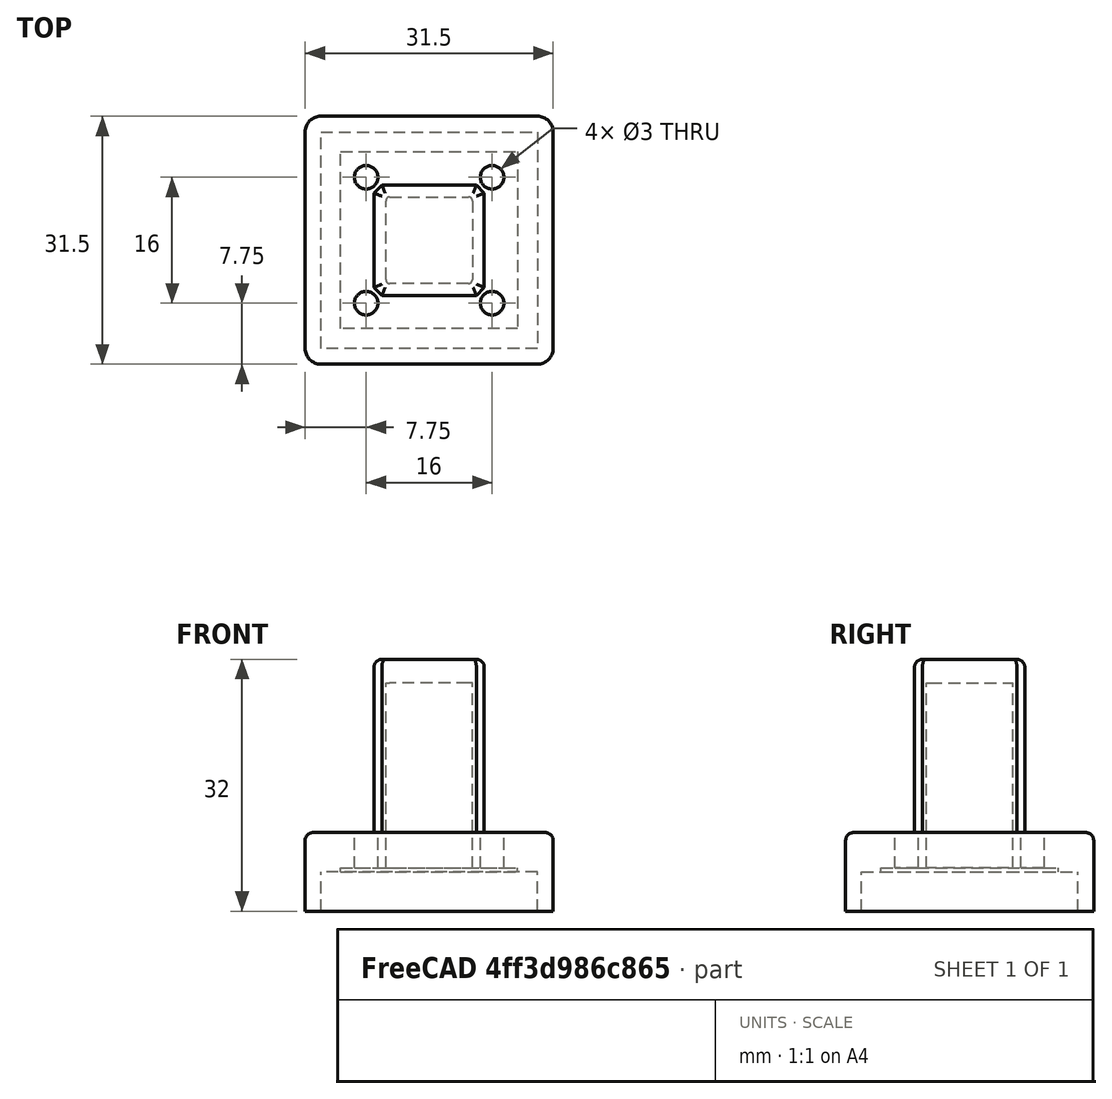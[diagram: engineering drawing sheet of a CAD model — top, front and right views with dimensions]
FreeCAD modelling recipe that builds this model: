
FCSTD DOCUMENT  (FreeCAD 1.1R44874 (Git))
Label: hood1slim_10x10x20_B
objects: Sketcher::SketchObject×7, PartDesign::Pocket×3, PartDesign::Pad×2, PartDesign::Fillet×2, App::Point×1, PartDesign::Hole×1, PartDesign::Body×1, Mesh::Feature×1
note: 39 computed .brp shape members not serialized (recipe doc carries the construction recipe); baked Part::Feature solids carry a one-line shape summary decoded from their .brp

FEATURE [App::Point] Origin001
  Role = Origin
FEATURE [Sketcher::SketchObject] Sketch
  ArcFitTolerance = 1e-06
  AttachmentSupport = -> [Origin]
  ExternalTypes = [0]
  FullyConstrained = true
  MakeInternals = false
  MapMode = 5
  _ExternalGeoVersion = 1
  sketch-geometry (13):
    g0: LineSegment StartX=-13.75 StartY=-15.75 StartZ=0 EndX=13.75 EndY=-15.75 EndZ=0
    g1: LineSegment StartX=15.75 StartY=-13.75 StartZ=0 EndX=15.75 EndY=13.75 EndZ=0
    g2: LineSegment StartX=13.75 StartY=15.75 StartZ=0 EndX=-13.75 EndY=15.75 EndZ=0
    g3: LineSegment StartX=-15.75 StartY=13.75 StartZ=0 EndX=-15.75 EndY=-13.75 EndZ=0
    g4: GeomPoint [constr] X=0 Y=0 Z=0
    g5: ArcOfCircle CenterX=-13.75 CenterY=13.75 CenterZ=0 NormalX=0 NormalY=0 NormalZ=1 AngleXU=0 Radius=2 StartAngle=1.5708 EndAngle=3.14159
    g6: GeomPoint [constr] X=-15.75 Y=15.75 Z=0
    g7: ArcOfCircle CenterX=13.75 CenterY=13.75 CenterZ=0 NormalX=0 NormalY=0 NormalZ=1 AngleXU=0 Radius=2 StartAngle=0 EndAngle=1.5708
    g8: GeomPoint [constr] X=15.75 Y=15.75 Z=0
    g9: ArcOfCircle CenterX=13.75 CenterY=-13.75 CenterZ=0 NormalX=0 NormalY=0 NormalZ=1 AngleXU=0 Radius=2 StartAngle=4.71239 EndAngle=6.28319
    g10: GeomPoint [constr] X=15.75 Y=-15.75 Z=0
    g11: ArcOfCircle CenterX=-13.75 CenterY=-13.75 CenterZ=0 NormalX=0 NormalY=0 NormalZ=1 AngleXU=0 Radius=2 StartAngle=3.14159 EndAngle=4.71239
    g12: GeomPoint [constr] X=-15.75 Y=-15.75 Z=0
  constraints (28):
    c: Horizontal(g0)
    c: Horizontal(g2)
    c: Vertical(g1)
    c: Vertical(g3)
    c: Symmetric(g8,g12,g4)
    c: Distance(g10,g12) = 31.5
    c: Distance(g12,g6) = 31.5
    c: Coincident(g4,g-1)
    c: PointOnObject(g6,g3)
    c: PointOnObject(g6,g2)
    c: Tangent(g3,g5) = -1.5708
    c: Tangent(g2,g5) = -1.5708
    c: Radius(g5) = 2
    c: PointOnObject(g8,g1)
    c: PointOnObject(g8,g2)
    c: Tangent(g1,g7) = -1.5708
    c: Tangent(g2,g7) = -1.5708
    c: PointOnObject(g10,g1)
    c: PointOnObject(g10,g0)
    c: Tangent(g1,g9) = -1.5708
    c: Tangent(g0,g9) = -1.5708
    c: PointOnObject(g12,g0)
    c: PointOnObject(g12,g3)
    c: Tangent(g0,g11) = -1.5708
    c: Tangent(g3,g11) = -1.5708
    c: Equal(g5,g7)
    c: Equal(g5,g11)
    c: Equal(g5,g9)
FEATURE [PartDesign::Pad] Pad
  Direction = (0,0,1)
  Length = 10
  Length2 = 10
  Profile = -> Sketch
  ReferenceAxis = -> Sketch [N_Axis]
  Refine = true
  SideType = 0
  Suppressed = false
  Type = 0
  Type2 = 0
FEATURE [Sketcher::SketchObject] Sketch001
  ArcFitTolerance = 1e-06
  AttachmentSupport = -> [Pad]
  ExternalTypes = [0]
  FullyConstrained = true
  MakeInternals = false
  MapMode = 5
  Placement = pos=(0,0,0) rot=(1,0,0;3.14159rad)
  _ExternalGeoVersion = 1
  sketch-geometry (5):
    g0: LineSegment StartX=-13.75 StartY=-13.75 StartZ=0 EndX=13.75 EndY=-13.75 EndZ=0
    g1: LineSegment StartX=13.75 StartY=-13.75 StartZ=0 EndX=13.75 EndY=13.75 EndZ=0
    g2: LineSegment StartX=13.75 StartY=13.75 StartZ=0 EndX=-13.75 EndY=13.75 EndZ=0
    g3: LineSegment StartX=-13.75 StartY=13.75 StartZ=0 EndX=-13.75 EndY=-13.75 EndZ=0
    g4: GeomPoint [constr] X=0 Y=0 Z=0
  constraints (12):
    c: Coincident(g0,g1)
    c: Coincident(g1,g2)
    c: Coincident(g2,g3)
    c: Coincident(g3,g0)
    c: Horizontal(g0)
    c: Horizontal(g2)
    c: Vertical(g1)
    c: Vertical(g3)
    c: Symmetric(g2,g0,g4)
    c: Distance(g1,g3) = 27.5
    c: Distance(g0,g2) = 27.5
    c: Coincident(g4,g-1)
FEATURE [PartDesign::Pocket] Pocket
  BaseFeature = -> Pad
  Direction = (0,0,1)
  Length = 5
  Length2 = 5
  Profile = -> Sketch001
  ReferenceAxis = -> Sketch001 [N_Axis]
  Refine = true
  SideType = 0
  Suppressed = false
  Type = 0
  Type2 = 0
FEATURE [Sketcher::SketchObject] Sketch002
  ArcFitTolerance = 1e-06
  AttachmentSupport = -> [Pocket]
  ExternalTypes = [0]
  FullyConstrained = true
  MakeInternals = false
  MapMode = 5
  Placement = pos=(0,0,5) rot=(1,0,0;3.14159rad)
  _ExternalGeoVersion = 1
  sketch-geometry (5):
    g0: LineSegment StartX=-11.25 StartY=-11.25 StartZ=0 EndX=11.25 EndY=-11.25 EndZ=0
    g1: LineSegment StartX=11.25 StartY=-11.25 StartZ=0 EndX=11.25 EndY=11.25 EndZ=0
    g2: LineSegment StartX=11.25 StartY=11.25 StartZ=0 EndX=-11.25 EndY=11.25 EndZ=0
    g3: LineSegment StartX=-11.25 StartY=11.25 StartZ=0 EndX=-11.25 EndY=-11.25 EndZ=0
    g4: GeomPoint [constr] X=0 Y=0 Z=0
  constraints (12):
    c: Coincident(g0,g1)
    c: Coincident(g1,g2)
    c: Coincident(g2,g3)
    c: Coincident(g3,g0)
    c: Horizontal(g0)
    c: Horizontal(g2)
    c: Vertical(g1)
    c: Vertical(g3)
    c: Symmetric(g2,g0,g4)
    c: Distance(g1,g3) = 22.5
    c: Distance(g0,g2) = 22.5
    c: Coincident(g4,g-1)
FEATURE [PartDesign::Pocket] Pocket001
  BaseFeature = -> Pocket
  Direction = (0,0,1)
  Length = 0.5
  Length2 = 5
  Profile = -> Sketch002
  ReferenceAxis = -> Sketch002 [N_Axis]
  Refine = true
  SideType = 0
  Suppressed = false
  Type = 0
  Type2 = 0
FEATURE [Sketcher::SketchObject] Sketch003
  ArcFitTolerance = 1e-06
  AttachmentSupport = -> [Pocket001]
  ExternalTypes = [0]
  FullyConstrained = true
  MakeInternals = false
  MapMode = 5
  Placement = pos=(0,0,5.5) rot=(1,0,0;3.14159rad)
  _ExternalGeoVersion = 1
  sketch-geometry (4):
    g0: Circle CenterX=8 CenterY=8 CenterZ=0 NormalX=0 NormalY=0 NormalZ=1 AngleXU=0 Radius=1.5
    g1: Circle CenterX=-8 CenterY=8 CenterZ=0 NormalX=0 NormalY=0 NormalZ=1 AngleXU=0 Radius=1.5
    g2: Circle CenterX=-8 CenterY=-8 CenterZ=0 NormalX=0 NormalY=0 NormalZ=1 AngleXU=0 Radius=1.5
    g3: Circle CenterX=8 CenterY=-8 CenterZ=0 NormalX=0 NormalY=0 NormalZ=1 AngleXU=0 Radius=1.5
  constraints (9):
    c: Diameter(g0) = 3
    c: DistanceY(g-1,g0) = 8
    c: DistanceX(g-1,g0) = 8
    c: Equal(g0,g1)
    c: Equal(g0,g2)
    c: Equal(g0,g3)
    c: Symmetric(g1,g3,g-1)
    c: Symmetric(g0,g3,g-1)
    c: Symmetric(g2,g3,g-2)
FEATURE [PartDesign::Hole] Hole
  BaseFeature = -> Pocket001
  BaseProfileType = 7
  CustomThreadClearance = 0
  Depth = 15
  DepthType = 0
  Diameter = 3
  DrillForDepth = false
  DrillPoint = 1
  DrillPointAngle = 118
  HoleCutCountersinkAngle = 90
  HoleCutCustomValues = false
  HoleCutDepth = 0
  HoleCutDiameter = 0
  HoleCutType = 0
  ModelThread = false
  Profile = -> Sketch003
  Refine = true
  Suppressed = false
  Tapered = false
  TaperedAngle = 90
  ThreadClass = 0
  ThreadDepth = 15
  ThreadDepthType = 0
  ThreadDiameter = 3
  ThreadDirection = 0
  ThreadFit = 0
  ThreadSize = 0
  ThreadType = 0
  Threaded = false
  UseCustomThreadClearance = false
FEATURE [Sketcher::SketchObject] Sketch004
  ArcFitTolerance = 1e-06
  AttachmentSupport = -> [Hole]
  ExternalGeometry = -> [Sketch002]
  ExternalTypes = [0,0,0,0]
  FullyConstrained = true
  MakeInternals = false
  MapMode = 5
  Placement = pos=(0,0,5.5) rot=(1,0,0;3.14159rad)
  _ExternalGeoVersion = 1
  sketch-geometry (21):
    g0: GeomPoint [constr] X=0 Y=0 Z=0
    g1: LineSegment StartX=-11.25 StartY=-5.5 StartZ=0 EndX=-11.25 EndY=5.5 EndZ=0
    g2: LineSegment StartX=-11.25 StartY=5.5 StartZ=0 EndX=-7 EndY=5.5 EndZ=0
    g3: LineSegment StartX=-5.5 StartY=7 StartZ=0 EndX=-5.5 EndY=11.25 EndZ=0
    g4: LineSegment StartX=-5.5 StartY=11.25 StartZ=0 EndX=5.5 EndY=11.25 EndZ=0
    g5: LineSegment StartX=5.5 StartY=11.25 StartZ=0 EndX=5.5 EndY=7 EndZ=0
    g6: LineSegment StartX=7 StartY=5.5 StartZ=0 EndX=11.25 EndY=5.5 EndZ=0
    g7: LineSegment StartX=11.25 StartY=5.5 StartZ=0 EndX=11.25 EndY=-5.5 EndZ=0
    g8: LineSegment StartX=11.25 StartY=-5.5 StartZ=0 EndX=7 EndY=-5.5 EndZ=0
    g9: LineSegment StartX=5.5 StartY=-7 StartZ=0 EndX=5.5 EndY=-11.25 EndZ=0
    g10: LineSegment StartX=5.5 StartY=-11.25 StartZ=0 EndX=-5.5 EndY=-11.25 EndZ=0
    g11: LineSegment StartX=-5.5 StartY=-11.25 StartZ=0 EndX=-5.5 EndY=-7 EndZ=0
    g12: LineSegment StartX=-7 StartY=-5.5 StartZ=0 EndX=-11.25 EndY=-5.5 EndZ=0
    g13: ArcOfCircle CenterX=-7 CenterY=7 CenterZ=0 NormalX=0 NormalY=0 NormalZ=1 AngleXU=0 Radius=1.5 StartAngle=4.71239 EndAngle=6.28319
    g14: GeomPoint [constr] X=-5.5 Y=5.5 Z=0
    g15: ArcOfCircle CenterX=7 CenterY=7 CenterZ=0 NormalX=0 NormalY=0 NormalZ=1 AngleXU=0 Radius=1.5 StartAngle=3.14159 EndAngle=4.71239
    g16: GeomPoint [constr] X=5.5 Y=5.5 Z=0
    g17: ArcOfCircle CenterX=7 CenterY=-7 CenterZ=0 NormalX=0 NormalY=0 NormalZ=1 AngleXU=0 Radius=1.5 StartAngle=1.5708 EndAngle=3.14159
    g18: GeomPoint [constr] X=5.5 Y=-5.5 Z=0
    g19: ArcOfCircle CenterX=-7 CenterY=-7 CenterZ=0 NormalX=0 NormalY=0 NormalZ=1 AngleXU=0 Radius=1.5 StartAngle=0 EndAngle=1.5708
    g20: GeomPoint [constr] X=-5.5 Y=-5.5 Z=0
  constraints (46):
    c: Coincident(g0,g-1)
    c: Coincident(g1,g2)
    c: Horizontal(g2)
    c: Vertical(g3)
    c: Coincident(g3,g4)
    c: Coincident(g4,g5)
    c: Vertical(g5)
    c: Horizontal(g6)
    c: Coincident(g6,g7)
    c: Coincident(g7,g8)
    c: Vertical(g9)
    c: Coincident(g9,g10)
    c: Coincident(g10,g11)
    c: Coincident(g12,g1)
    c: Tangent(g4,g-3)
    c: Tangent(g1,g-4)
    c: Tangent(g7,g-6)
    c: Tangent(g10,g-5)
    c: DistanceY(g-1,g16) = 5.5
    c: DistanceX(g-1,g16) = 5.5
    c: Symmetric(g16,g18,g-1)
    c: Symmetric(g16,g14,g-2)
    c: Symmetric(g18,g20,g-2)
    c: Parallel(g6,g8)
    c: Parallel(g2,g12)
    c: Parallel(g9,g11)
    c: PointOnObject(g14,g3)
    c: PointOnObject(g14,g2)
    c: Tangent(g3,g13) = -1.5708
    c: Tangent(g2,g13) = -1.5708
    c: Radius(g13) = 1.5
    c: PointOnObject(g16,g5)
    c: PointOnObject(g16,g6)
    c: Tangent(g5,g15) = -1.5708
    c: Tangent(g6,g15) = -1.5708
    c: PointOnObject(g18,g8)
    c: PointOnObject(g18,g9)
    c: Tangent(g8,g17) = -1.5708
    c: Tangent(g9,g17) = -1.5708
    c: PointOnObject(g20,g12)
    c: PointOnObject(g20,g11)
    c: Tangent(g12,g19) = -1.5708
    c: Tangent(g11,g19) = -1.5708
    c: Equal(g13,g15)
    c: Equal(g13,g19)
    c: Equal(g13,g17)
FEATURE [Sketcher::SketchObject] Sketch005
  ArcFitTolerance = 1e-06
  AttachmentSupport = -> [Hole]
  ExternalTypes = [0]
  FullyConstrained = true
  MakeInternals = false
  MapMode = 5
  Placement = pos=(0,0,10) rot=(0,0,1;0rad)
  _ExternalGeoVersion = 1
  sketch-geometry (17):
    g0: LineSegment StartX=-6 StartY=-7 StartZ=0 EndX=6 EndY=-7 EndZ=0
    g1: LineSegment StartX=7 StartY=-6 StartZ=0 EndX=7 EndY=6 EndZ=0
    g2: LineSegment StartX=6 StartY=7 StartZ=0 EndX=-6 EndY=7 EndZ=0
    g3: LineSegment StartX=-7 StartY=6 StartZ=0 EndX=-7 EndY=-6 EndZ=0
    g4: GeomPoint [constr] X=0 Y=0 Z=0
    g5: ArcOfCircle [constr] CenterX=-6 CenterY=6 CenterZ=0 NormalX=0 NormalY=0 NormalZ=1 AngleXU=0 Radius=1 StartAngle=1.5708 EndAngle=3.14159
    g6: GeomPoint [constr] X=-7 Y=7 Z=0
    g7: LineSegment StartX=-6 StartY=7 StartZ=0 EndX=-7 EndY=6 EndZ=0
    g8: ArcOfCircle [constr] CenterX=6 CenterY=-6 CenterZ=0 NormalX=0 NormalY=0 NormalZ=1 AngleXU=0 Radius=1 StartAngle=4.71239 EndAngle=6.28319
    g9: GeomPoint [constr] X=7 Y=-7 Z=0
    g10: LineSegment StartX=6 StartY=-7 StartZ=0 EndX=7 EndY=-6 EndZ=0
    g11: ArcOfCircle [constr] CenterX=6 CenterY=6 CenterZ=0 NormalX=0 NormalY=0 NormalZ=1 AngleXU=0 Radius=1 StartAngle=0 EndAngle=1.5708
    g12: GeomPoint [constr] X=7 Y=7 Z=0
    g13: LineSegment StartX=7 StartY=6 StartZ=0 EndX=6 EndY=7 EndZ=0
    g14: ArcOfCircle [constr] CenterX=-6 CenterY=-6 CenterZ=0 NormalX=0 NormalY=0 NormalZ=1 AngleXU=0 Radius=1 StartAngle=3.14159 EndAngle=4.71239
    g15: GeomPoint [constr] X=-7 Y=-7 Z=0
    g16: LineSegment StartX=-7 StartY=-6 StartZ=0 EndX=-6 EndY=-7 EndZ=0
  constraints (36):
    c: Horizontal(g0)
    c: Horizontal(g2)
    c: Vertical(g1)
    c: Vertical(g3)
    c: Symmetric(g12,g15,g4)
    c: Distance(g9,g15) = 14
    c: Distance(g15,g6) = 14
    c: Coincident(g4,g-1)
    c: PointOnObject(g6,g3)
    c: PointOnObject(g6,g2)
    c: Tangent(g3,g5) = -1.5708
    c: Tangent(g2,g5) = -1.5708
    c: Coincident(g7,g3)
    c: Coincident(g7,g2)
    c: PointOnObject(g9,g1)
    c: PointOnObject(g9,g0)
    c: Tangent(g1,g8) = -1.5708
    c: Tangent(g0,g8) = -1.5708
    c: Coincident(g10,g1)
    c: Coincident(g10,g0)
    c: Equal(g7,g10)
    c: DistanceY(g4,g3) = 6
    c: PointOnObject(g12,g2)
    c: PointOnObject(g12,g1)
    c: Tangent(g2,g11) = -1.5708
    c: Tangent(g1,g11) = -1.5708
    c: Coincident(g13,g2)
    c: Coincident(g13,g1)
    c: Equal(g7,g13)
    c: PointOnObject(g15,g0)
    c: PointOnObject(g15,g3)
    c: Tangent(g0,g14) = -1.5708
    c: Tangent(g3,g14) = -1.5708
    c: Coincident(g16,g0)
    c: Coincident(g16,g3)
    c: Equal(g7,g16)
FEATURE [PartDesign::Pad] Pad001
  BaseFeature = -> Hole
  Direction = (0,0,1)
  Length = 22
  Length2 = 10
  Profile = -> Sketch005
  ReferenceAxis = -> Sketch005 [N_Axis]
  Refine = true
  SideType = 0
  Suppressed = false
  Type = 0
  Type2 = 0
FEATURE [Sketcher::SketchObject] Sketch006
  ArcFitTolerance = 1e-06
  AttachmentSupport = -> [Pad001]
  ExternalTypes = [0]
  FullyConstrained = true
  MakeInternals = false
  MapMode = 5
  Placement = pos=(0,0,5.5) rot=(1,0,0;3.14159rad)
  _ExternalGeoVersion = 1
  sketch-geometry (10):
    g0: LineSegment StartX=-5 StartY=-5.5 StartZ=0 EndX=5 EndY=-5.5 EndZ=0
    g1: LineSegment StartX=5.5 StartY=-5 StartZ=0 EndX=5.5 EndY=5 EndZ=0
    g2: LineSegment StartX=5 StartY=5.5 StartZ=0 EndX=-5 EndY=5.5 EndZ=0
    g3: LineSegment StartX=-5.5 StartY=5 StartZ=0 EndX=-5.5 EndY=-5 EndZ=0
    g4: ArcOfCircle CenterX=-5 CenterY=-5 CenterZ=0 NormalX=0 NormalY=0 NormalZ=1 AngleXU=0 Radius=0.5 StartAngle=3.14159 EndAngle=4.71239
    g5: ArcOfCircle CenterX=5 CenterY=-5 CenterZ=0 NormalX=0 NormalY=0 NormalZ=1 AngleXU=0 Radius=0.5 StartAngle=4.71239 EndAngle=6.28319
    g6: ArcOfCircle CenterX=5 CenterY=5 CenterZ=0 NormalX=0 NormalY=0 NormalZ=1 AngleXU=0 Radius=0.5 StartAngle=0 EndAngle=1.5708
    g7: ArcOfCircle CenterX=-5 CenterY=5 CenterZ=0 NormalX=0 NormalY=0 NormalZ=1 AngleXU=0 Radius=0.5 StartAngle=1.5708 EndAngle=3.14159
    g8: GeomPoint [constr] X=5.5 Y=5.5 Z=0
    g9: GeomPoint [constr] X=0 Y=0 Z=0
  constraints (22):
    c: Tangent(g0,g4) = -1.5708
    c: Tangent(g0,g5) = -1.5708
    c: Tangent(g1,g5) = -1.5708
    c: Tangent(g1,g6) = -1.5708
    c: Tangent(g2,g6) = -1.5708
    c: Tangent(g2,g7) = -1.5708
    c: Tangent(g3,g7) = -1.5708
    c: Tangent(g3,g4) = -1.5708
    c: Horizontal(g0)
    c: Horizontal(g2)
    c: Vertical(g1)
    c: Vertical(g3)
    c: Equal(g4,g5)
    c: Equal(g5,g6)
    c: Equal(g6,g7)
    c: Symmetric(g2,g0,g9)
    c: PointOnObject(g8,g1)
    c: PointOnObject(g8,g2)
    c: Distance(g1,g3) = 11
    c: Distance(g0,g2) = 11
    c: Radius(g5) = 0.5
    c: Coincident(g9,g-1)
FEATURE [PartDesign::Pocket] Pocket002
  BaseFeature = -> Pad001
  Direction = (0,0,1)
  Length = 23.5
  Length2 = 5
  Profile = -> Sketch006
  ReferenceAxis = -> Sketch006 [N_Axis]
  Refine = true
  SideType = 0
  Suppressed = false
  Type = 0
  Type2 = 0
FEATURE [PartDesign::Fillet] Fillet
  Base = -> Pocket002 [Face29]
  BaseFeature = -> Pocket002
  Radius = 1
  Refine = true
  SupportTransform = false
  Suppressed = false
  UseAllEdges = false
FEATURE [PartDesign::Fillet] Fillet001
  Base = -> Fillet [Edge18]
  BaseFeature = -> Fillet
  Radius = 1
  Refine = true
  SupportTransform = false
  Suppressed = false
  UseAllEdges = false
FEATURE [PartDesign::Body] Body
  AllowCompound = true
  Group = -> [Sketch,Pad,Sketch001,Pocket,Sketch002,Pocket001,Sketch003,Hole,Sketch004,Sketch005,Pad001,Sketch006,Pocket002,Fillet,Fillet001]
  Origin = -> Origin
  Tip = -> Fillet001
FEATURE [Mesh::Feature] Mesh  label="Body (Meshed)"
